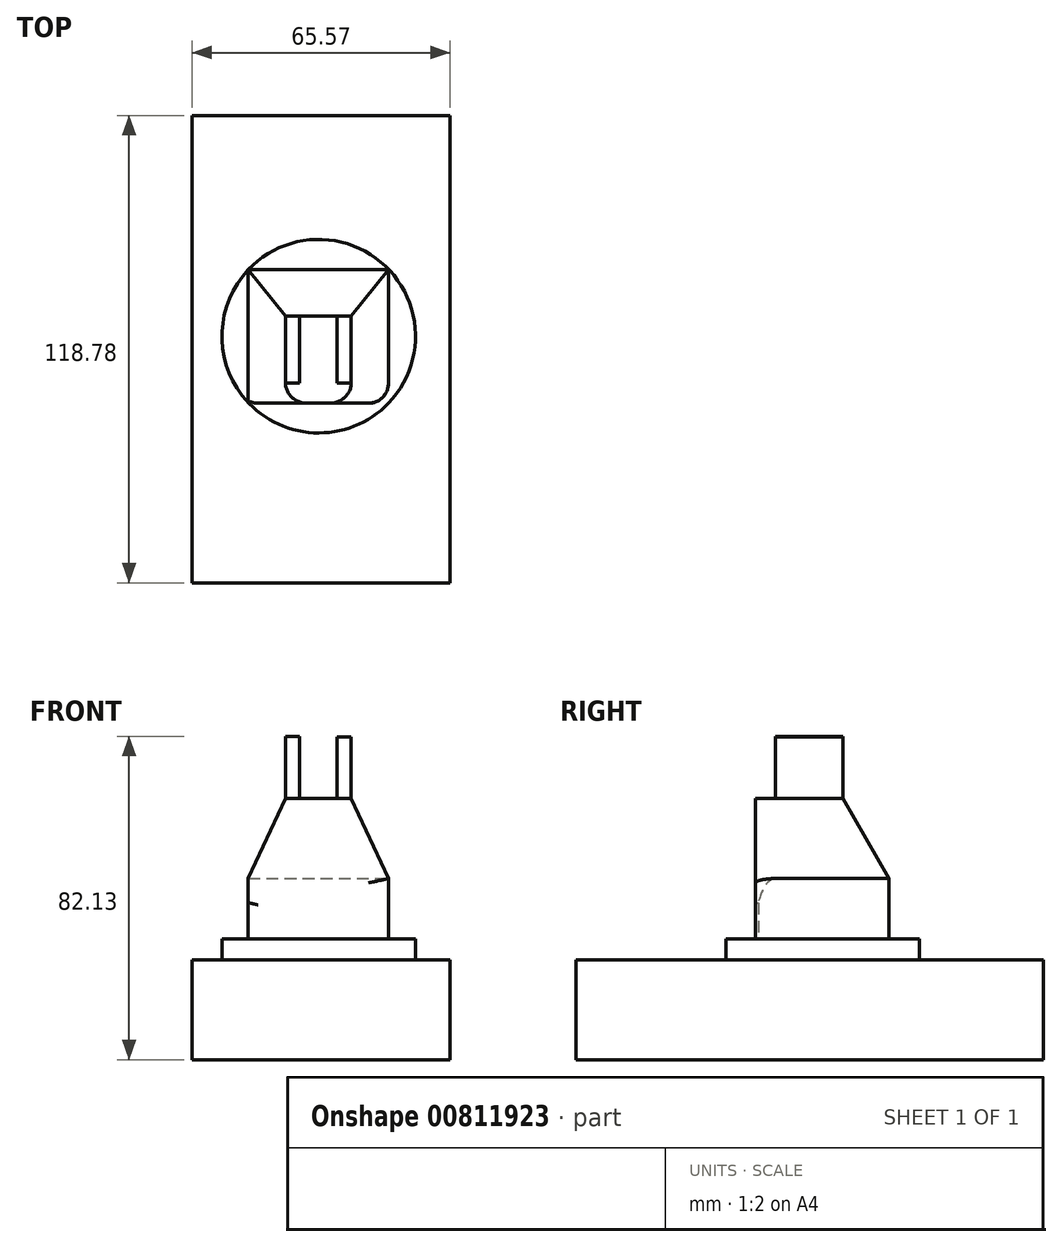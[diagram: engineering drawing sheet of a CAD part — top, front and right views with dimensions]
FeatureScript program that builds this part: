
annotation { "Feature Type Name" : "Feature", "Feature Type Description" : "" }
export const myFeature = defineFeature(function(context is Context, id is Id, definition is map)
    precondition{}
    {
        {
            var Q0;
            Q0=qCreatedBy(makeId("Top.planeOp"),FACE);
            var sketch = newSketch(context, id + "F0", { "sketchPlane" : qUnion([Q0])});
            skLineSegment(sketch, "E0.bottom", {"start": v(-32.2, 56.1) * mm, "end": v(33.36, 56.1) * mm});
            skLineSegment(sketch, "E0.top", {"start": v(-32.2, -62.7) * mm, "end": v(33.36, -62.7) * mm});
            skLineSegment(sketch, "E0.left", {"start": v(-32.2, 56.1) * mm, "end": v(-32.2, -62.7) * mm});
            skLineSegment(sketch, "E0.right", {"start": v(33.36, 56.1) * mm, "end": v(33.36, -62.7) * mm});
            skSolve(sketch);
        }
        {
            var Q0;
            Q0 = qSketchRegion(id + "F0", true);
            var Q1;
            Q1=makeQuery(id+"F0.imprint","IMPRINT",FACE,{"disambiguationData":[TD([[makeQuery(id+"F0.imprint","IMPRINT",EDGE,{"derivedFrom":sQuery(id+"F0.wireOp",EDGE,"E0.bottom")}),-1.0]])]});
            extrude(context, id + "F1", {"entities" : qUnion([Q0, Q1]), "depth" : 25.4 * mm, "offsetDistance" : 25.4 * mm});
        }
        {
            var Q0;
            Q0=makeQuery(id+"F1.opExtrude","CAP_FACE",FACE,{"disambiguationData":[OSD([sQuery(id+"F0.wireOp",EDGE,"E0.bottom"),sQuery(id+"F0.wireOp",EDGE,"E0.top"),sQuery(id+"F0.wireOp",EDGE,"E0.left"),sQuery(id+"F0.wireOp",EDGE,"E0.right")])],"isStart":false});
            var sketch = newSketch(context, id + "F2", { "sketchPlane" : qUnion([Q0])});
            skCircle(sketch, "E1", {"center": v(0, 0) * mm, "radius": 24.58 * mm});
            skSolve(sketch);
        }
        {
            var Q0;
            Q0=makeQuery(id+"F2.imprint","IMPRINT",FACE,{"disambiguationData":[TD([[makeQuery(id+"F2.imprint","IMPRINT",EDGE,{"derivedFrom":sQuery(id+"F2.wireOp",EDGE,"E1")}),1.0]])]});
            extrude(context, id + "F3", {"entities" : qUnion([Q0]), "operationType" : NewBodyOperationType.ADD, "depth" : 5.28 * mm, "offsetDistance" : 25.4 * mm});
        }
        {
            var Q0;
            Q0=makeQuery(id+"F3.opExtrude","CAP_FACE",FACE,{"disambiguationData":[OSD([sQuery(id+"F2.wireOp",EDGE,"E1")])],"isStart":false});
            var sketch = newSketch(context, id + "F4", { "sketchPlane" : qUnion([Q0])});
            skLineSegment(sketch, "E2.bottom", {"start": v(-17.9, 16.86) * mm, "end": v(17.72, 16.86) * mm});
            skLineSegment(sketch, "E2.top", {"start": v(-17.9, -17.04) * mm, "end": v(17.72, -17.04) * mm});
            skLineSegment(sketch, "E2.left", {"start": v(-17.9, 16.86) * mm, "end": v(-17.9, -17.04) * mm});
            skLineSegment(sketch, "E2.right", {"start": v(17.72, 16.86) * mm, "end": v(17.72, -17.04) * mm});
            skSolve(sketch);
        }
        {
            var Q0;
            {var subQ1=sQuery(id+"F4.wireOp",EDGE,"E2.bottom");Q0=makeQuery(id+"F4.imprint","IMPRINT",FACE,{"disambiguationData":[TD([[makeQuery(id+"F4.imprint","IMPRINT",EDGE,{"derivedFrom":subQ1}),-1.0]])]});}
            extrude(context, id + "F5", {"entities" : qUnion([Q0]), "operationType" : NewBodyOperationType.ADD, "depth" : 35.67 * mm, "offsetDistance" : 25.4 * mm});
        }
        {
            var Q0;
            Q0=makeQuery(id+"F5.opExtrude","CAP_EDGE",EDGE,{"disambiguationData":[OSD([sQuery(id+"F4.wireOp",EDGE,"E2.right")])],"isStart":false});
            var Q1;
            Q1=makeQuery(id+"F5.opExtrude","CAP_EDGE",EDGE,{"disambiguationData":[OSD([sQuery(id+"F4.wireOp",EDGE,"E2.left")])],"isStart":false});
            chamfer(context, id + "F6", {"entities" : qUnion([Q0, Q1]), "chamferType" : ChamferType.OFFSET_ANGLE, "width" : 20.32 * mm, "oppositeDirection" : false, "angle" : 25 * degree, "tangentPropagation" : true});
        }
        {
            var Q0;
            Q0=makeQuery(id+"F5.opExtrude","CAP_EDGE",EDGE,{"disambiguationData":[OSD([sQuery(id+"F4.wireOp",EDGE,"E2.bottom")])],"isStart":false});
            chamfer(context, id + "F7", {"entities" : qUnion([Q0]), "chamferType" : ChamferType.OFFSET_ANGLE, "width" : 20.32 * mm, "oppositeDirection" : false, "angle" : 30 * degree, "tangentPropagation" : true});
        }
        {
            var Q0;
            Q0=makeQuery(id+"F6.opChamfer","BLEND_EDGE",EDGE,{"blendedFrom":[makeQuery(id+"F5.opExtrude","CAP_EDGE",EDGE,{"disambiguationData":[OSD([sQuery(id+"F4.wireOp",EDGE,"E2.right")])],"isStart":false}),makeQuery(id+"F5.opExtrude","SWEPT_FACE",FACE,{"disambiguationData":[OSD([sQuery(id+"F4.wireOp",EDGE,"E2.top")])]})],"blendedInto":[makeQuery(id+"F5.opExtrude","SWEPT_FACE",FACE,{"disambiguationData":[OSD([sQuery(id+"F4.wireOp",EDGE,"E2.top")])]})]});
            var Q1;
            Q1=makeQuery(id+"F5.opExtrude","SWEPT_EDGE",EDGE,{"disambiguationData":[OSD([sQuery(id+"F2.wireOp",EDGE,"E1"),sQuery(id+"F4.wireOp",EDGE,"E2.top"),sQuery(id+"F4.wireOp",EDGE,"E2.right")])]});
            var Q2;
            Q2=makeQuery(id+"F5.opExtrude","SWEPT_EDGE",EDGE,{"disambiguationData":[OSD([sQuery(id+"F2.wireOp",EDGE,"E1"),sQuery(id+"F4.wireOp",EDGE,"E2.top")])]});
            var Q3;
            Q3=makeQuery(id+"F6.opChamfer","BLEND_EDGE",EDGE,{"blendedFrom":[makeQuery(id+"F5.opExtrude","CAP_EDGE",EDGE,{"disambiguationData":[OSD([sQuery(id+"F4.wireOp",EDGE,"E2.left")])],"isStart":false}),makeQuery(id+"F5.opExtrude","SWEPT_FACE",FACE,{"disambiguationData":[OSD([sQuery(id+"F4.wireOp",EDGE,"E2.top")])]})],"blendedInto":[makeQuery(id+"F5.opExtrude","SWEPT_FACE",FACE,{"disambiguationData":[OSD([sQuery(id+"F4.wireOp",EDGE,"E2.top")])]})]});
            fillet(context, id + "F8", {"entities" : qUnion([Q0, Q1, Q2, Q3]), "radius" : 5.08 * mm, "tangentPropagation" : true, "allowEdgeOverflow" : false});
        }
        {
            var Q0;
            Q0=makeQuery(id+"F5.opExtrude","CAP_FACE",FACE,{"disambiguationData":[OSD([sQuery(id+"F2.wireOp",EDGE,"E1"),sQuery(id+"F4.wireOp",EDGE,"E2.bottom"),sQuery(id+"F4.wireOp",EDGE,"E2.top"),sQuery(id+"F4.wireOp",EDGE,"E2.left"),sQuery(id+"F4.wireOp",EDGE,"E2.right")])],"isStart":false});
            var sketch = newSketch(context, id + "F9", { "sketchPlane" : qUnion([Q0])});
            skLineSegment(sketch, "E3.bottom", {"start": v(8.25, 5.13) * mm, "end": v(4.66, 5.13) * mm});
            skLineSegment(sketch, "E3.top", {"start": v(8.25, -11.96) * mm, "end": v(4.66, -11.96) * mm});
            skLineSegment(sketch, "E3.left", {"start": v(8.25, 5.13) * mm, "end": v(8.25, -11.96) * mm});
            skLineSegment(sketch, "E3.right", {"start": v(4.66, 5.13) * mm, "end": v(4.66, -11.96) * mm});
            skSolve(sketch);
        }
        {
            var Q0;
            Q0=makeQuery(id+"F9.imprint","IMPRINT",FACE,{"disambiguationData":[TD([[makeQuery(id+"F9.imprint","IMPRINT",EDGE,{"derivedFrom":sQuery(id+"F9.wireOp",EDGE,"E3.bottom")}),1.0]])]});
            extrude(context, id + "F10", {"entities" : qUnion([Q0]), "operationType" : NewBodyOperationType.ADD, "depth" : 15.6 * mm, "offsetDistance" : 25.4 * mm});
        }
        {
            var Q0;
            Q0=makeQuery(id+"F5.opExtrude","CAP_FACE",FACE,{"disambiguationData":[OSD([sQuery(id+"F2.wireOp",EDGE,"E1"),sQuery(id+"F4.wireOp",EDGE,"E2.bottom"),sQuery(id+"F4.wireOp",EDGE,"E2.top"),sQuery(id+"F4.wireOp",EDGE,"E2.left"),sQuery(id+"F4.wireOp",EDGE,"E2.right")])],"isStart":false});
            var sketch = newSketch(context, id + "F11", { "sketchPlane" : qUnion([Q0])});
            skPoint(sketch, "E4.oppositeSnap0", {"position": v(-2.96, -11.96) * mm});
            skLineSegment(sketch, "E4.bottom", {"start": v(-8.42, 5.13) * mm, "end": v(-4.85, 5.13) * mm});
            skLineSegment(sketch, "E4.top", {"start": v(-8.42, -11.96) * mm, "end": v(-4.85, -11.96) * mm});
            skLineSegment(sketch, "E4.left", {"start": v(-8.42, 5.13) * mm, "end": v(-8.42, -11.96) * mm});
            skLineSegment(sketch, "E4.right", {"start": v(-4.85, 5.13) * mm, "end": v(-4.85, -11.96) * mm});
            skSolve(sketch);
        }
        {
            var Q0;
            Q0 = qSketchRegion(id + "F11", true);
            var Q1;
            Q1=makeQuery(id+"F11.imprint","IMPRINT",FACE,{"disambiguationData":[TD([[makeQuery(id+"F11.imprint","IMPRINT",EDGE,{"derivedFrom":sQuery(id+"F11.wireOp",EDGE,"E4.bottom")}),1.0]])]});
            extrude(context, id + "F12", {"entities" : qUnion([Q0, Q1]), "operationType" : NewBodyOperationType.ADD, "depth" : 15.79 * mm, "offsetDistance" : 25.4 * mm});
        }
    });
